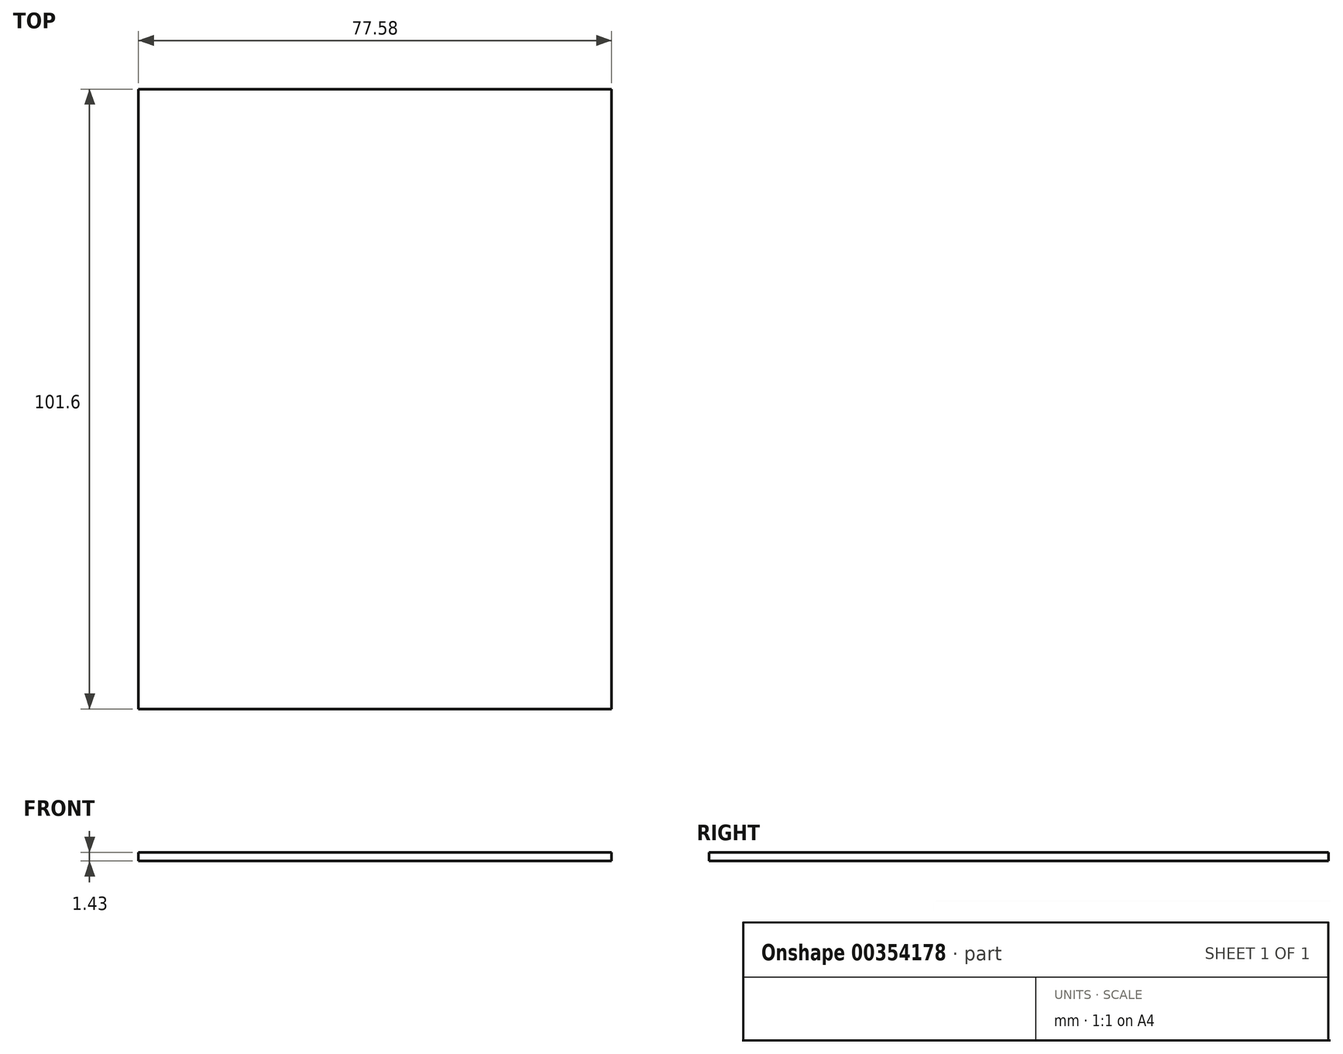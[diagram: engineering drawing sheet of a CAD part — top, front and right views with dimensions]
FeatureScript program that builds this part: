
annotation { "Feature Type Name" : "Feature", "Feature Type Description" : "" }
export const myFeature = defineFeature(function(context is Context, id is Id, definition is map)
    precondition{}
    {
        {
            var Q0;
            Q0=qCreatedBy(makeId("Front.planeOp"),FACE);
            var sketch = newSketch(context, id + "F0", { "sketchPlane" : qUnion([Q0])});
            skLineSegment(sketch, "E0.bottom", {"start": v(-49.06, 14.69) * mm, "end": v(28.52, 14.69) * mm});
            skLineSegment(sketch, "E0.top", {"start": v(-49.06, 13.26) * mm, "end": v(28.52, 13.26) * mm});
            skLineSegment(sketch, "E0.left", {"start": v(-49.06, 14.69) * mm, "end": v(-49.06, 13.26) * mm});
            skLineSegment(sketch, "E0.right", {"start": v(28.52, 14.69) * mm, "end": v(28.52, 13.26) * mm});
            skSolve(sketch);
        }
        {
            var Q0;
            Q0 = qSketchRegion(id + "F0", true);
            extrude(context, id + "F1", {"entities" : qUnion([Q0]), "depth" : 101.6 * mm});
        }
    });
